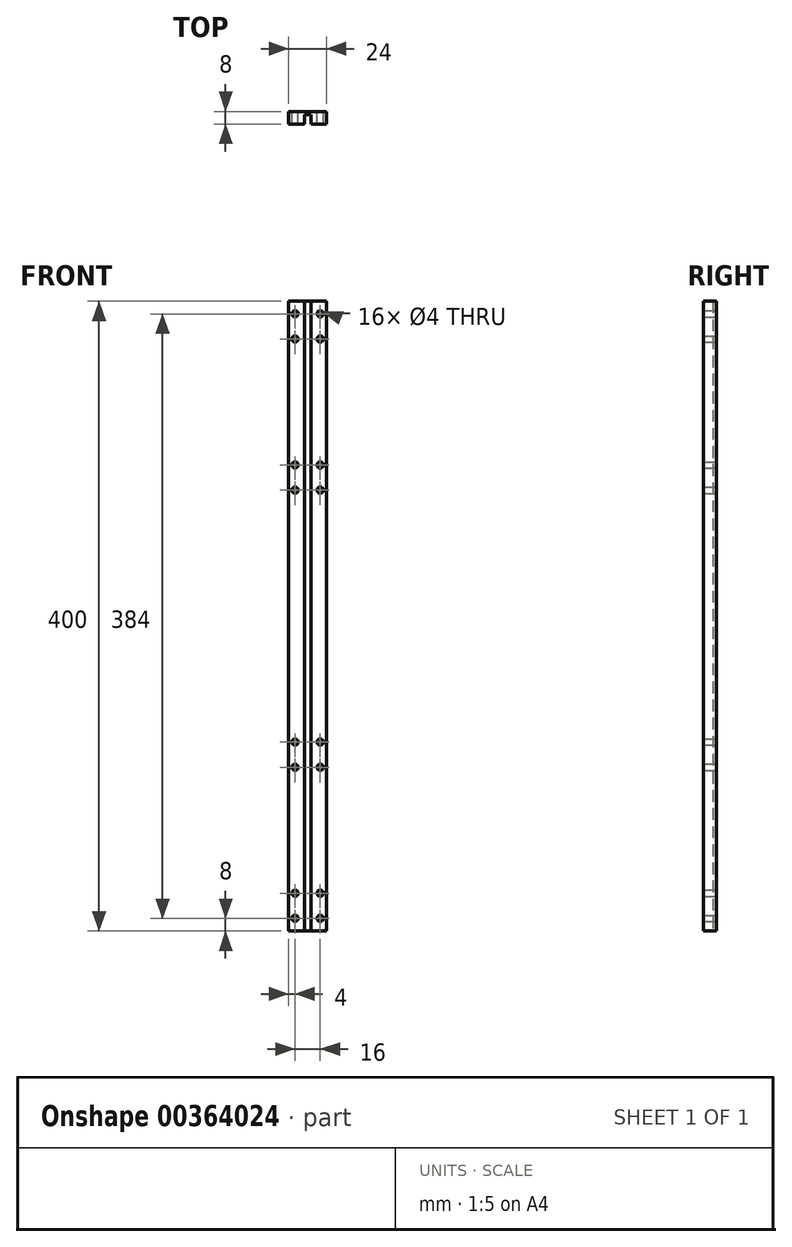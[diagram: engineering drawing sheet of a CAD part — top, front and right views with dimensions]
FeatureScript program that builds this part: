
annotation { "Feature Type Name" : "Feature", "Feature Type Description" : "" }
export const myFeature = defineFeature(function(context is Context, id is Id, definition is map)
    precondition{}
    {
        {
            var Q0;
            Q0=qCreatedBy(makeId("Top.planeOp"),FACE);
            var sketch = newSketch(context, id + "F0", { "sketchPlane" : qUnion([Q0])});
            skLineSegment(sketch, "E0.top", {"start": v(12, 4) * mm, "end": v(-12, 4) * mm});
            skLineSegment(sketch, "E0.left", {"start": v(12, -4) * mm, "end": v(12, 4) * mm});
            skLineSegment(sketch, "E0.right", {"start": v(-12, -4) * mm, "end": v(-12, 4) * mm});
            skPoint(sketch, "E0.middle", {"position": v(0, 0) * mm});
            skLineSegment(sketch, "E1", {"start": v(-12, -4) * mm, "end": v(-2, -4) * mm});
            skLineSegment(sketch, "E2", {"start": v(-2, -4) * mm, "end": v(-2, 2) * mm});
            skLineSegment(sketch, "E3", {"start": v(-2, 2) * mm, "end": v(2, 2) * mm});
            skLineSegment(sketch, "E4", {"start": v(2, 2) * mm, "end": v(2, -4) * mm});
            skLineSegment(sketch, "E5", {"start": v(2, -4) * mm, "end": v(12, -4) * mm});
            skSolve(sketch);
        }
        {
            var Q0;
            Q0=qSketchRegion(id+"F0",true);
            extrude(context, id + "F1", {"entities" : qUnion([Q0]), "depth" : 400 * mm});
        }
        {
            var Q0;
            Q0=makeQuery(id+"F1.opExtrude","SWEPT_FACE",FACE,{"disambiguationData":[OSD([sQuery(id+"F0.wireOp",EDGE,"E0.top")])]});
            var sketch = newSketch(context, id + "F2", { "sketchPlane" : qUnion([Q0])});
            skLineSegment(sketch, "E6", {"start": v(-8, 0) * mm, "end": v(-8, 8) * mm, "construction": true});
            skCircle(sketch, "E7", {"center": v(-8, 8) * mm, "radius": 2 * mm});
            skLineSegment(sketch, "E8", {"start": v(12, 200) * mm, "end": v(-12, 200) * mm, "construction": true});
            skCircle(sketch, "E9.0.1.0", {"center": v(-8, 24) * mm, "radius": 2 * mm});
            skCircle(sketch, "E9.1.0.0", {"center": v(8, 8) * mm, "radius": 2 * mm});
            skCircle(sketch, "E9.1.1.0", {"center": v(8, 24) * mm, "radius": 2 * mm});
            skLineSegment(sketch, "E9.direction1", {"start": v(-8, 8) * mm, "end": v(8, 8) * mm, "construction": true});
            skLineSegment(sketch, "E9.direction2", {"start": v(-8, 8) * mm, "end": v(-8, 24) * mm, "construction": true});
            skCircle(sketch, "E10", {"center": v(-8, 104) * mm, "radius": 2 * mm});
            skCircle(sketch, "E11.0.1.0", {"center": v(-8, 120) * mm, "radius": 2 * mm});
            skCircle(sketch, "E11.1.0.0", {"center": v(8, 104) * mm, "radius": 2 * mm});
            skCircle(sketch, "E11.1.1.0", {"center": v(8, 120) * mm, "radius": 2 * mm});
            skLineSegment(sketch, "E11.direction1", {"start": v(-8, 104) * mm, "end": v(8, 104) * mm, "construction": true});
            skLineSegment(sketch, "E11.direction2", {"start": v(-8, 104) * mm, "end": v(-8, 120) * mm, "construction": true});
            skCircle(sketch, "E12.MirrorC", {"center": v(-8, 392) * mm, "radius": 2 * mm});
            skCircle(sketch, "E13.MirrorC", {"center": v(-8, 296) * mm, "radius": 2 * mm});
            skCircle(sketch, "E14.MirrorC", {"center": v(-8, 280) * mm, "radius": 2 * mm});
            skCircle(sketch, "E15.MirrorC", {"center": v(8, 392) * mm, "radius": 2 * mm});
            skCircle(sketch, "E16.MirrorC", {"center": v(-8, 376) * mm, "radius": 2 * mm});
            skCircle(sketch, "E17.MirrorC", {"center": v(8, 296) * mm, "radius": 2 * mm});
            skLineSegment(sketch, "E18.MirrorCS", {"start": v(-8, 400) * mm, "end": v(-8, 392) * mm, "construction": true});
            skLineSegment(sketch, "E19.MirrorCS", {"start": v(-8, 296) * mm, "end": v(-8, 280) * mm, "construction": true});
            skCircle(sketch, "E20.MirrorC", {"center": v(8, 376) * mm, "radius": 2 * mm});
            skCircle(sketch, "E21.MirrorC", {"center": v(8, 280) * mm, "radius": 2 * mm});
            skLineSegment(sketch, "E22.MirrorCS", {"start": v(-8, 296) * mm, "end": v(8, 296) * mm, "construction": true});
            skLineSegment(sketch, "E23.MirrorCS", {"start": v(-8, 392) * mm, "end": v(8, 392) * mm, "construction": true});
            skLineSegment(sketch, "E24.MirrorCS", {"start": v(-8, 392) * mm, "end": v(-8, 376) * mm, "construction": true});
            skSolve(sketch);
        }
        {
            var Q0;
            Q0=qSketchRegion(id+"F2",true);
            extrude(context, id + "F3", {"entities" : qUnion([Q0]), "operationType" : NewBodyOperationType.REMOVE, "oppositeDirection" : true, "depth" : 25 * mm});
        }
    });
